# Revit family: NAU_Naughtone_Stng_Ruby1
name_source: partatom
category: Furniture
revit_build: Autodesk Revit 2018 (Build: 20170223_1515(x64)
units: mm (PartAtom-declared; Revit-internal decimal feet)

## family parameters
Always vertical = Yes
Cut with Voids When Loaded = No
OmniClass Number = 23.40.20.00
OmniClass Title = General Furniture and Specialties
Room Calculation Point = No
Shared = Yes
Work Plane-Based = No

## types (3) — shared parameters
Assembly Code = E2020200
AssetType = Movable
BIMObjectName = NAU_Naughtone_Seating_Ruby
Category = Pr_40_50_12 : Chairs, seats and benches
Color = Various
DurationUnit = year
Finish = Plastic Shell in 8 RAL colours
IfcExportAs = IfcFurnishingElementType
IfcExportType = CHAIR
Keynote = Pr_40_50_12
MainColor = Various
ManufacturerAddress = Knaresborough Tech Park, Manse Lane, Knaresborough, HG5 8LF
ManufacturerName = Naughtone
ManufacturerURL = www.naughtone.com
Material = Steel/Polypropylene
NBSDescription = Seating
NBSReference = 45-35-72/352
Name = Seating_Ruby_Naughtone
NominalHeight = 785 mm
NominalLength = 610 mm  [stored 2.00131 ft]
ProductInformation = www.naughtone.com/products/ruby/
Revision = 0
Shape = Rectangular
SustainabilityPerformance = FSC certified. FISP certified. ISO 14001
URL = www.naughtone.com
Uniclass2015Code = Pr_40_50_12
Uniclass2015Title = Chairs, seats and benches
Version = 1
WarrantyDescription = Request warranty information from naughtone
WarrantyDurationLabor = 7
WarrantyDurationParts = 7
WarrantyDurationUnit = year

## per-type parameters (varying)
| type | Description | IsRUBYCHB4L | IsRUBYCHBDL | IsRUBYCHBSL | Model | ModelNumber | ModelReference | NominalWidth | Size |
| Ruby Chair 4 Leg Base_RUBYCHB4L | Ruby Chair 4 Leg Base | Yes | No | No | RUBYCHB4L | RUBYCHB4L | Ruby Chair 4 Leg Base | 540 mm  [stored 1.77165 ft] | 610 x 540 x 785mm |
| Ruby Chair Sled Base_RUBYCHBSL | Ruby Chair Sled Base | No | No | Yes | RUBYCHBSL | RUBYCHBSL | Ruby Chair Sled Base | 530 mm  [stored 1.73885 ft] | 610 x 530 x 785mm |
| Ruby Chair Dowel Base_RUBYCHBDL | Ruby Chair Dowel Base | No | Yes | No | RUBYCHBDL | RUBYCHBDL | Ruby Chair Dowel Base | 530 mm  [stored 1.73885 ft] | 610 x 530 x 785mm |

note: [stored X ft] marks values corroborated as IEEE doubles in the binary element streams (Revit-internal decimal feet)

## geometry (parser evidence)
native form markers: Sweep x5
no freeform markers — native parametric forms only
